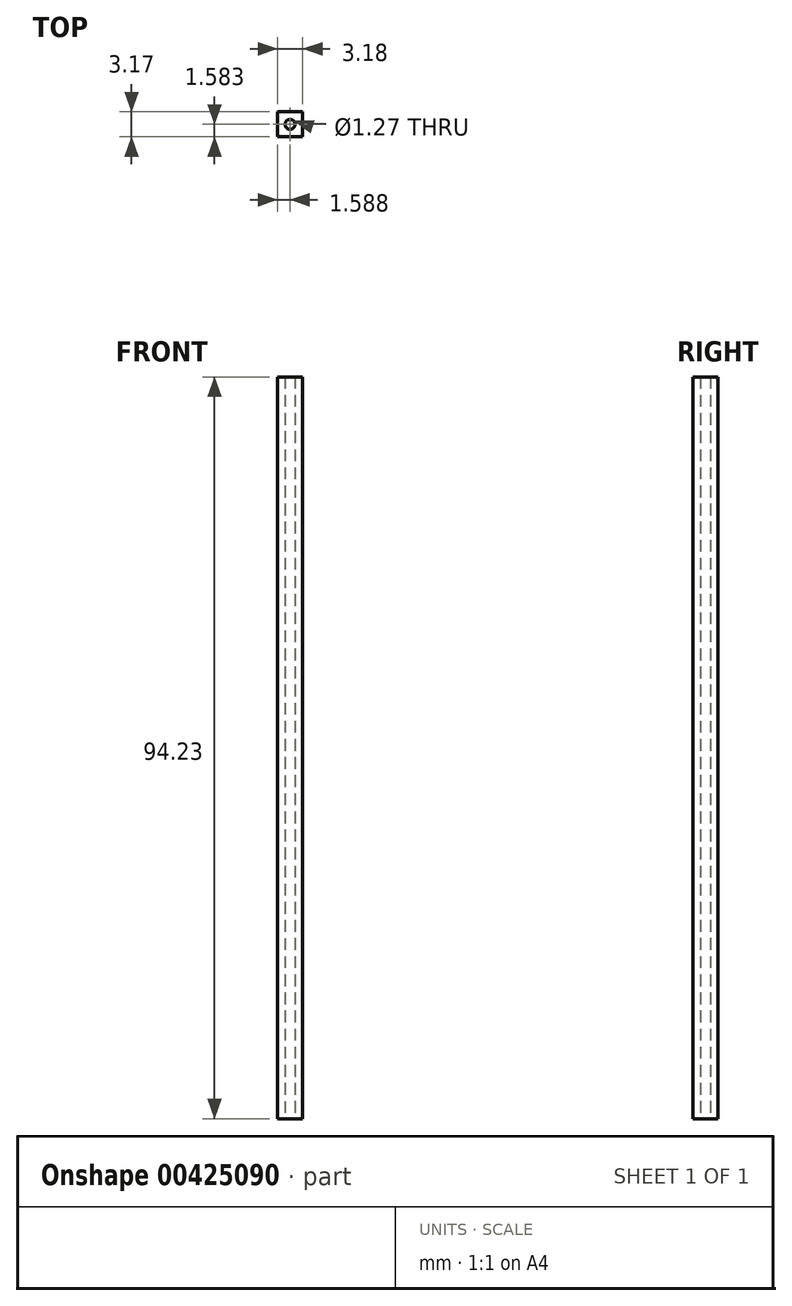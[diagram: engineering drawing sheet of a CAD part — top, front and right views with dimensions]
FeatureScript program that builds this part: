
annotation { "Feature Type Name" : "Feature", "Feature Type Description" : "" }
export const myFeature = defineFeature(function(context is Context, id is Id, definition is map)
    precondition{}
    {
        {
            var Q0;
            Q0=qCreatedBy(makeId("Front.planeOp"),FACE);
            var sketch = newSketch(context, id + "F0", { "sketchPlane" : qUnion([Q0])});
            skLineSegment(sketch, "E0.bottom", {"start": v(-46.22, 68.35) * mm, "end": v(-43.04, 68.35) * mm});
            skLineSegment(sketch, "E0.top", {"start": v(-46.22, -25.88) * mm, "end": v(-43.04, -25.88) * mm});
            skLineSegment(sketch, "E0.left", {"start": v(-46.22, 68.35) * mm, "end": v(-46.22, -25.88) * mm});
            skLineSegment(sketch, "E0.right", {"start": v(-43.04, 68.35) * mm, "end": v(-43.04, -25.88) * mm});
            skSolve(sketch);
        }
        {
            var Q0;
            Q0 = qSketchRegion(id + "F0", true);
            extrude(context, id + "F1", {"entities" : qUnion([Q0]), "depth" : 3.17 * mm});
        }
        {
            var Q0;
            Q0=makeQuery(id+"F1.opExtrude","SWEPT_FACE",FACE,{"disambiguationData":[OSD([sQuery(id+"F0.wireOp",EDGE,"E0.top")])]});
            var sketch = newSketch(context, id + "F2", { "sketchPlane" : qUnion([Q0])});
            skCircle(sketch, "E1", {"center": v(-44.63, 1.59) * mm, "radius": 0.64 * mm});
            skPoint(sketch, "E1.centerSnap0", {"position": v(-46.22, 1.59) * mm});
            skPoint(sketch, "E1.centerSnap1", {"position": v(-44.63, 3.18) * mm});
            skSolve(sketch);
        }
        {
            var Q0;
            Q0 = qSketchRegion(id + "F2", true);
            extrude(context, id + "F3", {"entities" : qUnion([Q0]), "operationType" : NewBodyOperationType.REMOVE, "oppositeDirection" : true, "depth" : 105.54 * mm});
        }
    });
